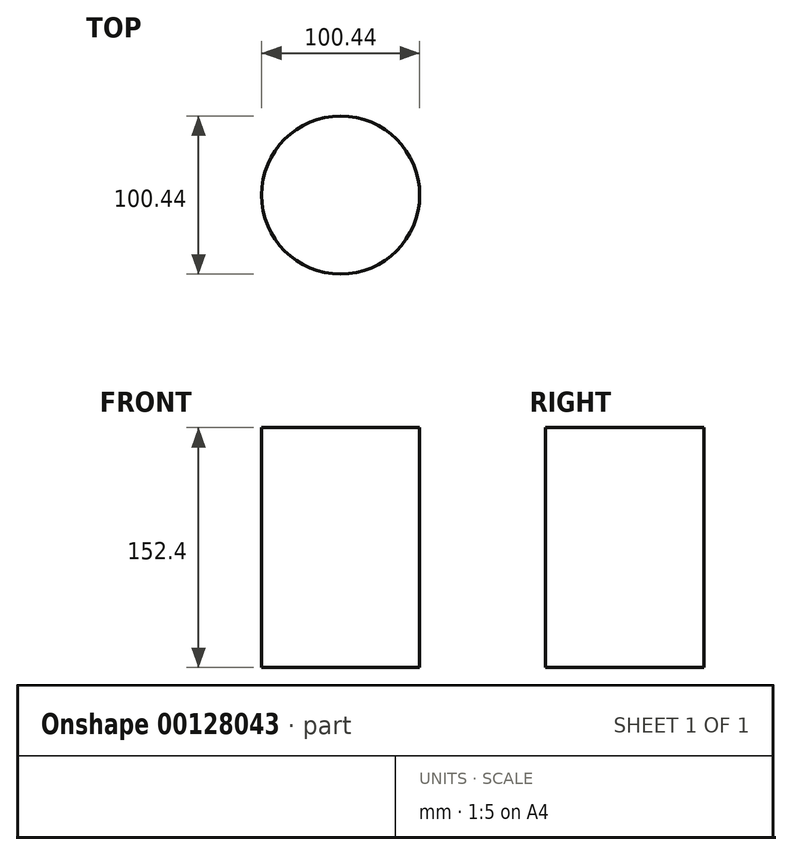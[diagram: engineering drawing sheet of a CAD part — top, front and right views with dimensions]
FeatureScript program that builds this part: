
annotation { "Feature Type Name" : "Feature", "Feature Type Description" : "" }
export const myFeature = defineFeature(function(context is Context, id is Id, definition is map)
    precondition{}
    {
        {
            var Q0;
            Q0=qCreatedBy(makeId("Top.planeOp"),FACE);
            var sketch = newSketch(context, id + "F0", { "sketchPlane" : qUnion([Q0])});
            skCircle(sketch, "E0", {"center": v(0, 0) * mm, "radius": 50.22 * mm});
            skSolve(sketch);
        }
        {
            var Q0;
            Q0 = qSketchRegion(id + "F0", true);
            extrude(context, id + "F1", {"entities" : qUnion([Q0]), "depth" : 152.4 * mm});
        }
    });
